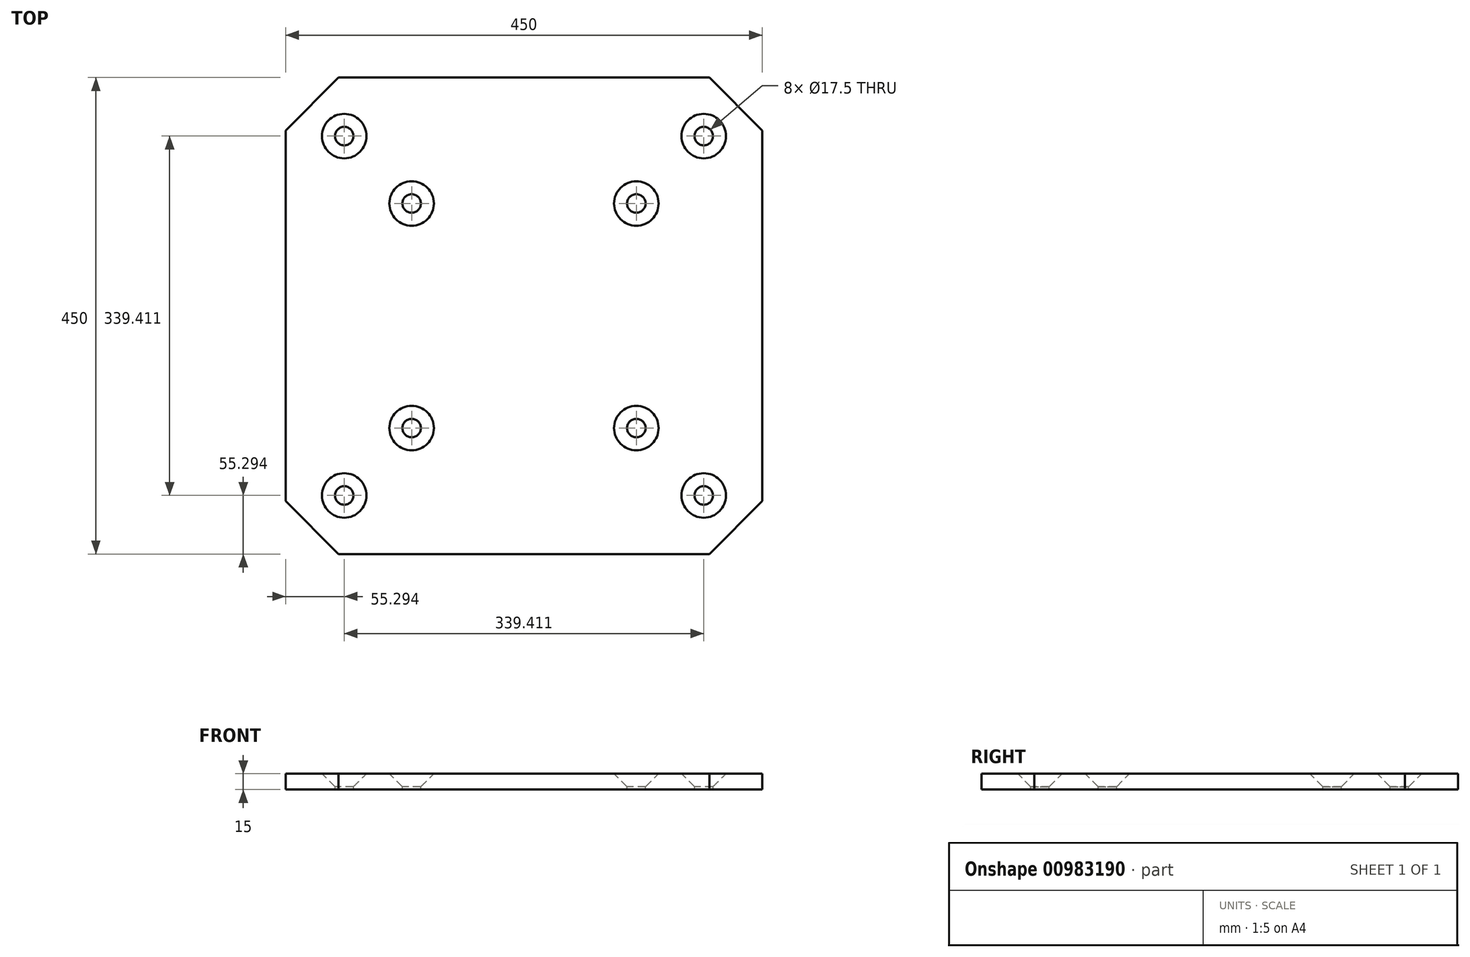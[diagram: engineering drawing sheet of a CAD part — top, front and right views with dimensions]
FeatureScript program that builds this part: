
annotation { "Feature Type Name" : "Feature", "Feature Type Description" : "" }
export const myFeature = defineFeature(function(context is Context, id is Id, definition is map)
    precondition{}
    {
        {
            var Q0;
            Q0=qCreatedBy(makeId("Top.planeOp"),FACE);
            var sketch = newSketch(context, id + "F0", { "sketchPlane" : qUnion([Q0])});
            skLineSegment(sketch, "E0.bottom", {"start": v(225, -225) * mm, "end": v(-225, -225) * mm});
            skLineSegment(sketch, "E0.top", {"start": v(225, 225) * mm, "end": v(-225, 225) * mm});
            skLineSegment(sketch, "E0.left", {"start": v(225, -225) * mm, "end": v(225, 225) * mm});
            skLineSegment(sketch, "E0.right", {"start": v(-225, -225) * mm, "end": v(-225, 225) * mm});
            skPoint(sketch, "E0.middle", {"position": v(0, 0) * mm});
            skSolve(sketch);
        }
        {
            var Q0;
            Q0=makeQuery(id+"F0.imprint","IMPRINT",FACE,{"disambiguationData":[TD([[makeQuery(id+"F0.imprint","IMPRINT",EDGE,{"derivedFrom":sQuery(id+"F0.wireOp",EDGE,"E0.bottom")}),-1.0]])]});
            extrude(context, id + "F1", {"entities" : qUnion([Q0]), "depth" : 15 * mm, "offsetDistance" : 25 * mm});
        }
        {
            var Q0;
            Q0=makeQuery(id+"F1.opExtrude","CAP_FACE",FACE,{"disambiguationData":[OSD([sQuery(id+"F0.wireOp",EDGE,"E0.bottom"),sQuery(id+"F0.wireOp",EDGE,"E0.top"),sQuery(id+"F0.wireOp",EDGE,"E0.left"),sQuery(id+"F0.wireOp",EDGE,"E0.right")])],"isStart":false});
            var sketch = newSketch(context, id + "F2", { "sketchPlane" : qUnion([Q0])});
            skPoint(sketch, "E1", {"position": v(-169.7, -169.7) * mm});
            skLineSegment(sketch, "E2", {"start": v(-169.7, -169.7) * mm, "end": v(169.7, 169.7) * mm});
            skLineSegment(sketch, "E3", {"start": v(-169.7, 169.7) * mm, "end": v(169.7, -169.7) * mm});
            skPoint(sketch, "E4", {"position": v(-169.7, 169.7) * mm});
            skPoint(sketch, "E5", {"position": v(169.7, 169.7) * mm});
            skPoint(sketch, "E6", {"position": v(169.7, -169.7) * mm});
            skPoint(sketch, "E7", {"position": v(-106.07, -106.07) * mm});
            skPoint(sketch, "E8", {"position": v(106.07, -106.07) * mm});
            skPoint(sketch, "E9", {"position": v(-106.07, 106.07) * mm});
            skPoint(sketch, "E10", {"position": v(106.07, 106.07) * mm});
            skSolve(sketch);
        }
        {
            var Q0;
            Q0=sQuery(id+"F2.wireOp",VERTEX,"E5");
            var Q1;
            Q1=sQuery(id+"F2.wireOp",VERTEX,"E6");
            var Q2;
            Q2=sQuery(id+"F2.wireOp",VERTEX,"E1");
            var Q3;
            Q3=sQuery(id+"F2.wireOp",VERTEX,"E4");
            var Q4;
            Q4=sQuery(id+"F2.wireOp",VERTEX,"E9");
            var Q5;
            Q5=sQuery(id+"F2.wireOp",VERTEX,"E10");
            var Q6;
            Q6=sQuery(id+"F2.wireOp",VERTEX,"E8");
            var Q7;
            Q7=sQuery(id+"F2.wireOp",VERTEX,"E7");
            var Q8;
            Q8=makeQuery(id+"F1.opExtrude","SWEPT_BODY",BODY,{"disambiguationData":[OSD([sQuery(id+"F0.wireOp",EDGE,"E0.bottom"),sQuery(id+"F0.wireOp",EDGE,"E0.top"),sQuery(id+"F0.wireOp",EDGE,"E0.left"),sQuery(id+"F0.wireOp",EDGE,"E0.right")])]});
            hole(context, id + "F3", {"style" : HoleStyle.C_SINK, "endStyle" : HoleEndStyle.BLIND, "standardTappedOrClearance" : lookupTablePath({ "standard" : "ISO", "fit" : "Loose", "engagement" : "75%", "pitch" : "2.5 mm", "size" : "M20", "type" : "Tapped" }), "standardBlindInLast" : lookupTablePath({ "fit" : "Loose", "standard" : "ISO", "engagement" : "75%", "pitch" : "2.5 mm", "size" : "M20", "type" : "Clearance & tapped" }), "holeDiameter" : 17.5 * mm, "cSinkDiameter" : 42 * mm, "cSinkAngle" : 90 * degree, "majorDiameter" : 20 * mm, "showTappedDepth" : true, "holeDepth" : 57.5 * mm, "isTappedThrough" : true, "tappedDepth" : 50 * mm, "tapClearance" : 3, "locations" : qUnion([Q0, Q1, Q2, Q3, Q4, Q5, Q6, Q7]), "scope" : qUnion([Q8])});
        }
        {
            var Q0;
            Q0=makeQuery(id+"F1.opExtrude","SWEPT_EDGE",EDGE,{"disambiguationData":[OSD([sQuery(id+"F0.wireOp",EDGE,"E0.bottom"),sQuery(id+"F0.wireOp",EDGE,"E0.left")])]});
            var Q1;
            Q1=makeQuery(id+"F1.opExtrude","SWEPT_EDGE",EDGE,{"disambiguationData":[OSD([sQuery(id+"F0.wireOp",EDGE,"E0.top"),sQuery(id+"F0.wireOp",EDGE,"E0.left")])]});
            var Q2;
            Q2=makeQuery(id+"F1.opExtrude","SWEPT_EDGE",EDGE,{"disambiguationData":[OSD([sQuery(id+"F0.wireOp",EDGE,"E0.top"),sQuery(id+"F0.wireOp",EDGE,"E0.right")])]});
            var Q3;
            Q3=makeQuery(id+"F1.opExtrude","SWEPT_EDGE",EDGE,{"disambiguationData":[OSD([sQuery(id+"F0.wireOp",EDGE,"E0.bottom"),sQuery(id+"F0.wireOp",EDGE,"E0.right")])]});
            chamfer(context, id + "F4", {"entities" : qUnion([Q0, Q1, Q2, Q3]), "width" : 50 * mm, "tangentPropagation" : true});
        }
    });
